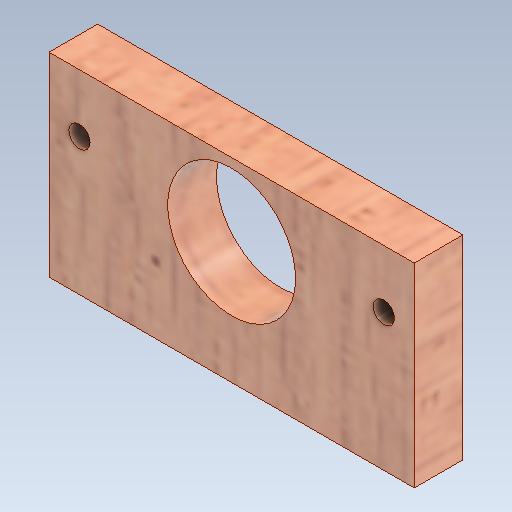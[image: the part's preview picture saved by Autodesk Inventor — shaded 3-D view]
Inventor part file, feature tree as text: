
AUTODESK INVENTOR PART (.ipt)
format: ipt  version: 2020 (Build 240168000, 168)  size: 257,024 bytes
history: native  units: mm
features: extrude x3, sketch x3, direct_edit x1, move_body x1
ambient origin geometry x8: Origin, YZ Plane, XZ Plane, XY Plane, X Axis, Y Axis, Z Axis, Center Point
bodies: Solid1 (feature_tree)
feature tree (8):
  extrude  "Extrusion1"  Depth=60.0mm
  extrude  "Extrusion2"  Depth=8.0mm
  extrude  "Extrusion3"  TaperAngle=0.0deg  [1 undecoded]
  direct_edit  "Direct Edit1"
  sketch  "Sketch1"  dims[d0=60.0mm d1=35.0mm]
  sketch  "Sketch2"  dims[d2=8.0mm d3=0.0mm d4=5.0mm]
  sketch  "Sketch3"  dims[d5=21.0mm d6=0.0mm d7=0.0mm d9=3.5mm d10=3.5mm d11=10.0mm d12=2.5mm d13=5.0mm d14=5.0mm d15=0.0mm d16=0.0mm d17=21.0mm d18=15.0mm d19=0.0mm d20=0.0mm d21=-3.0mm]
  move_body  "Move1"
note: 1 required parameter value undecoded (feature->parameter linkage not recoverable at this tier; creation-order binding heuristic only, values carry confidence <= 0.55)
